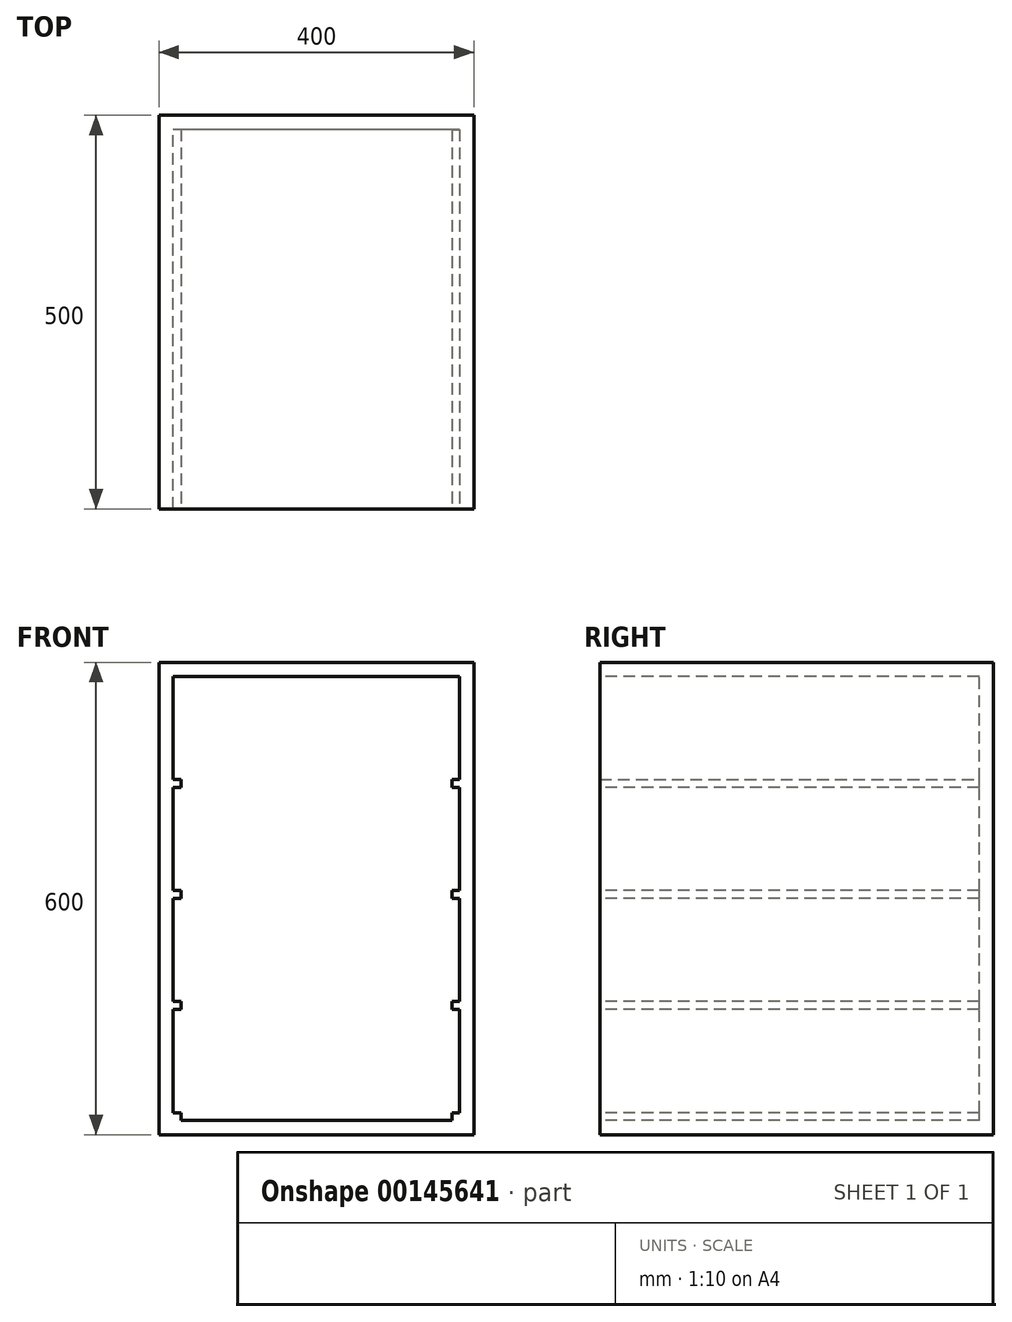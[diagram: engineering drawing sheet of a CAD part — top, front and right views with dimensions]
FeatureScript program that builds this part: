
annotation { "Feature Type Name" : "Feature", "Feature Type Description" : "" }
export const myFeature = defineFeature(function(context is Context, id is Id, definition is map)
    precondition{}
    {
        {
            var Q0;
            Q0=qCreatedBy(makeId("Front.planeOp"),FACE);
            var sketch = newSketch(context, id + "F0", { "sketchPlane" : qUnion([Q0])});
            skPoint(sketch, "E0.middle", {"position": v(0, 0) * mm});
            skLineSegment(sketch, "E1.bottom", {"start": v(200, -300) * mm, "end": v(-200, -300) * mm});
            skLineSegment(sketch, "E1.top", {"start": v(200, 300) * mm, "end": v(-200, 300) * mm});
            skLineSegment(sketch, "E1.left", {"start": v(200, -300) * mm, "end": v(200, 300) * mm});
            skLineSegment(sketch, "E1.right", {"start": v(-200, -300) * mm, "end": v(-200, 300) * mm});
            skSolve(sketch);
        }
        {
            var Q0;
            Q0=makeQuery(id+"F0.imprint","IMPRINT",FACE,{"disambiguationData":[TD([[makeQuery(id+"F0.imprint","IMPRINT",EDGE,{"derivedFrom":sQuery(id+"F0.wireOp",EDGE,"E1.bottom")}),-1.0]])]});
            extrude(context, id + "F1", {"entities" : qUnion([Q0]), "endBound" : BoundingType.SYMMETRIC, "depth" : 500 * mm});
        }
        {
            var Q0;
            Q0=makeQuery(id+"F1.opExtrude","CAP_FACE",FACE,{"disambiguationData":[OSD([sQuery(id+"F0.wireOp",EDGE,"E1.bottom"),sQuery(id+"F0.wireOp",EDGE,"E1.top"),sQuery(id+"F0.wireOp",EDGE,"E1.left"),sQuery(id+"F0.wireOp",EDGE,"E1.right")])],"isStart":false});
            var sketch = newSketch(context, id + "F2", { "sketchPlane" : qUnion([Q0])});
            skLineSegment(sketch, "E2.bottom", {"start": v(182, -282) * mm, "end": v(-182, -282) * mm});
            skLineSegment(sketch, "E2.top", {"start": v(182, 282) * mm, "end": v(-182, 282) * mm});
            skLineSegment(sketch, "E2.left", {"start": v(182, -282) * mm, "end": v(182, 282) * mm});
            skLineSegment(sketch, "E2.right", {"start": v(-182, -282) * mm, "end": v(-182, 282) * mm});
            skPoint(sketch, "E2.middle", {"position": v(0, 0) * mm});
            skSolve(sketch);
        }
        {
            var Q0;
            Q0=makeQuery(id+"F2.imprint","IMPRINT",FACE,{"disambiguationData":[TD([[makeQuery(id+"F2.imprint","IMPRINT",EDGE,{"derivedFrom":sQuery(id+"F2.wireOp",EDGE,"E2.bottom")}),-1.0]])]});
            extrude(context, id + "F3", {"entities" : qUnion([Q0]), "operationType" : NewBodyOperationType.REMOVE, "oppositeDirection" : true, "depth" : 482 * mm});
        }
        {
            var Q0;
            Q0=makeQuery(id+"F3.boolean.opBoolean","COPY",FACE,{"derivedFrom":makeQuery(id+"F3.opExtrude","SWEPT_FACE",FACE,{"disambiguationData":[OSD([sQuery(id+"F2.wireOp",EDGE,"E2.right")])]})});
            var sketch = newSketch(context, id + "F4", { "sketchPlane" : qUnion([Q0])});
            skLineSegment(sketch, "E3.bottom", {"start": v(-250, 151) * mm, "end": v(232, 151) * mm});
            skLineSegment(sketch, "E3.top", {"start": v(-250, 141) * mm, "end": v(232, 141) * mm});
            skLineSegment(sketch, "E3.left", {"start": v(-250, 151) * mm, "end": v(-250, 141) * mm});
            skLineSegment(sketch, "E3.right", {"start": v(232, 151) * mm, "end": v(232, 141) * mm});
            skLineSegment(sketch, "E4.bottom", {"start": v(-250, 10) * mm, "end": v(232, 10) * mm});
            skLineSegment(sketch, "E4.top", {"start": v(-250, 0) * mm, "end": v(232, 0) * mm});
            skLineSegment(sketch, "E4.left", {"start": v(-250, 10) * mm, "end": v(-250, 0) * mm});
            skLineSegment(sketch, "E4.right", {"start": v(232, 10) * mm, "end": v(232, 0) * mm});
            skLineSegment(sketch, "E5.bottom", {"start": v(-250, -131) * mm, "end": v(232, -131) * mm});
            skLineSegment(sketch, "E5.top", {"start": v(-250, -141) * mm, "end": v(232, -141) * mm});
            skLineSegment(sketch, "E5.left", {"start": v(-250, -131) * mm, "end": v(-250, -141) * mm});
            skLineSegment(sketch, "E5.right", {"start": v(232, -131) * mm, "end": v(232, -141) * mm});
            skLineSegment(sketch, "E6.bottom", {"start": v(-250, -272) * mm, "end": v(232, -272) * mm});
            skLineSegment(sketch, "E6.top", {"start": v(-250, -282) * mm, "end": v(232, -282) * mm});
            skLineSegment(sketch, "E6.left", {"start": v(-250, -272) * mm, "end": v(-250, -282) * mm});
            skLineSegment(sketch, "E6.right", {"start": v(232, -272) * mm, "end": v(232, -282) * mm});
            skSolve(sketch);
        }
        {
            var Q0;
            Q0=makeQuery(id+"F4.imprint","IMPRINT",FACE,{"disambiguationData":[TD([[makeQuery(id+"F4.imprint","IMPRINT",EDGE,{"derivedFrom":sQuery(id+"F4.wireOp",EDGE,"E3.bottom")}),-1.0]])]});
            var Q1;
            Q1=makeQuery(id+"F4.imprint","IMPRINT",FACE,{"disambiguationData":[TD([[makeQuery(id+"F4.imprint","IMPRINT",EDGE,{"derivedFrom":sQuery(id+"F4.wireOp",EDGE,"E4.bottom")}),-1.0]])]});
            var Q2;
            Q2=makeQuery(id+"F4.imprint","IMPRINT",FACE,{"disambiguationData":[TD([[makeQuery(id+"F4.imprint","IMPRINT",EDGE,{"derivedFrom":sQuery(id+"F4.wireOp",EDGE,"E5.bottom")}),-1.0]])]});
            var Q3;
            Q3=makeQuery(id+"F4.imprint","IMPRINT",FACE,{"disambiguationData":[TD([[makeQuery(id+"F4.imprint","IMPRINT",EDGE,{"derivedFrom":sQuery(id+"F4.wireOp",EDGE,"E6.bottom")}),-1.0]])]});
            extrude(context, id + "F5", {"entities" : qUnion([Q0, Q1, Q2, Q3]), "operationType" : NewBodyOperationType.ADD, "depth" : 10 * mm});
        }
        {
            var Q0;
            Q0=makeQuery(id+"F3.boolean.opBoolean","COPY",FACE,{"derivedFrom":makeQuery(id+"F3.opExtrude","SWEPT_FACE",FACE,{"disambiguationData":[OSD([sQuery(id+"F2.wireOp",EDGE,"E2.left")])]})});
            var sketch = newSketch(context, id + "F6", { "sketchPlane" : qUnion([Q0])});
            skLineSegment(sketch, "E7.bottom", {"start": v(-232, -282) * mm, "end": v(250, -282) * mm});
            skLineSegment(sketch, "E7.top", {"start": v(-232, -272) * mm, "end": v(250, -272) * mm});
            skLineSegment(sketch, "E7.left", {"start": v(-232, -282) * mm, "end": v(-232, -272) * mm});
            skLineSegment(sketch, "E7.right", {"start": v(250, -282) * mm, "end": v(250, -272) * mm});
            skLineSegment(sketch, "E8.bottom", {"start": v(-232, -141) * mm, "end": v(250, -141) * mm});
            skLineSegment(sketch, "E8.top", {"start": v(-232, -131) * mm, "end": v(250, -131) * mm});
            skLineSegment(sketch, "E8.left", {"start": v(-232, -141) * mm, "end": v(-232, -131) * mm});
            skLineSegment(sketch, "E8.right", {"start": v(250, -141) * mm, "end": v(250, -131) * mm});
            skLineSegment(sketch, "E9.bottom", {"start": v(-232, 0) * mm, "end": v(250, 0) * mm});
            skLineSegment(sketch, "E9.top", {"start": v(-232, 10) * mm, "end": v(250, 10) * mm});
            skLineSegment(sketch, "E9.left", {"start": v(-232, 0) * mm, "end": v(-232, 10) * mm});
            skLineSegment(sketch, "E9.right", {"start": v(250, 0) * mm, "end": v(250, 10) * mm});
            skLineSegment(sketch, "E10.bottom", {"start": v(-232, 141) * mm, "end": v(250, 141) * mm});
            skLineSegment(sketch, "E10.top", {"start": v(-232, 151) * mm, "end": v(250, 151) * mm});
            skLineSegment(sketch, "E10.left", {"start": v(-232, 141) * mm, "end": v(-232, 151) * mm});
            skLineSegment(sketch, "E10.right", {"start": v(250, 141) * mm, "end": v(250, 151) * mm});
            skSolve(sketch);
        }
        {
            var Q0;
            Q0=makeQuery(id+"F6.imprint","IMPRINT",FACE,{"disambiguationData":[TD([[makeQuery(id+"F6.imprint","IMPRINT",EDGE,{"derivedFrom":sQuery(id+"F6.wireOp",EDGE,"E10.bottom")}),1.0]])]});
            var Q1;
            Q1=makeQuery(id+"F6.imprint","IMPRINT",FACE,{"disambiguationData":[TD([[makeQuery(id+"F6.imprint","IMPRINT",EDGE,{"derivedFrom":sQuery(id+"F6.wireOp",EDGE,"E9.bottom")}),1.0]])]});
            var Q2;
            Q2=makeQuery(id+"F6.imprint","IMPRINT",FACE,{"disambiguationData":[TD([[makeQuery(id+"F6.imprint","IMPRINT",EDGE,{"derivedFrom":sQuery(id+"F6.wireOp",EDGE,"E8.bottom")}),1.0]])]});
            var Q3;
            Q3=makeQuery(id+"F6.imprint","IMPRINT",FACE,{"disambiguationData":[TD([[makeQuery(id+"F6.imprint","IMPRINT",EDGE,{"derivedFrom":sQuery(id+"F6.wireOp",EDGE,"E7.bottom")}),1.0]])]});
            extrude(context, id + "F7", {"entities" : qUnion([Q0, Q1, Q2, Q3]), "operationType" : NewBodyOperationType.ADD, "depth" : 10 * mm});
        }
    });
